# Revit family: DockShelter_BlueGiant_BG400D
name_source: partatom
category: Specialty Equipment
units: mm (PartAtom-declared; Revit-internal decimal feet)

## family parameters
Always vertical = Yes
Cut with Voids When Loaded = No
Enable Cutting in Views = No
Maintain Annotation Orientation = No
Part Type = Normal
Room Calculation Point = No
Round Connector Dimension = Use Diameter
Shared = No
Work Plane-Based = Yes

## types (3) — shared parameters
Assembly Code = E1030300
Construction Details = http://www.arcat.com
Default Elevation = 4' - 0"
Description = Blue Giant BG400D Rigid Dock Shelter
Door Opening Height = 120' - 0"
Door Opening Width = 120' - 0"
Fabric Color = Fabric - Blue Giant - 22oz HT Blue Vinyl
Green Building-LEED = http://www.arcat.com
Installation_Fabricaton = http://www.bluegiant.com
Keynote = 11160
Manufacturer = Blue Giant Equipment Corp.
Manufacturer Fax = 905-457-2313
Manufacturer Website = http://www.bluegiant.com
Model = BG400D
Panel Material = Plastic - Blue Giant - Clear Poly
Product Data = http://www.arcat.com
Product Properties = http://www.arcat.com
Sales Information = http://www.bluegiant.com
Send Message = http://admin.arcat.com
SpecWizard = http://www.arcat.com
Specification = http://www.arcat.com
Standard Unit = Yes
Truck Guide Color = Fabric - Blue Giant - Yellow Guide
URL = http://www.bluegiant.com
zero-valued in all types: Expected Lifespan (Years), Maintenance Schedule (Months), Warranty Duration (Years)

## per-type parameters (varying)
| type | Projection |
| 48 inch Projection | 4' - 0" |
| 36 inch Projection | 3' - 0" |
| 24 inch Projection | 2' - 0" |

## geometry (parser evidence)
native form markers: Blend x10, Sweep x4
no freeform markers — native parametric forms only
